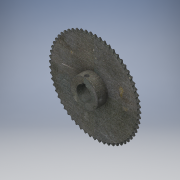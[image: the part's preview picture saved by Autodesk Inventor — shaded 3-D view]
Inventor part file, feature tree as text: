
AUTODESK INVENTOR PART (.ipt)
format: ipt  version: 2016 (Build 200138000, 138)  size: 3,148,288 bytes
history: native  units: in
note: dims shown in document units (in); Inventor stores cm internally (conversion verified against a paired STEP export)
features: pattern_circular x2, plane x1, sketch x1, other x1
ambient origin geometry x8: Origin, YZ Plane, XZ Plane, XY Plane, X Axis, Y Axis, Z Axis, Center Point
bodies: Solid1 (feature_tree), Solid2 (feature_tree), Solid3 (feature_tree)
feature tree (5):
  plane  "Work Plane1"
  sketch  "Sketch2"  dims[d1=7.1925in]
  pattern_circular  "CirPattern2"
  other  "Cut-Extrude7"
  pattern_circular  "CirPattern3"
